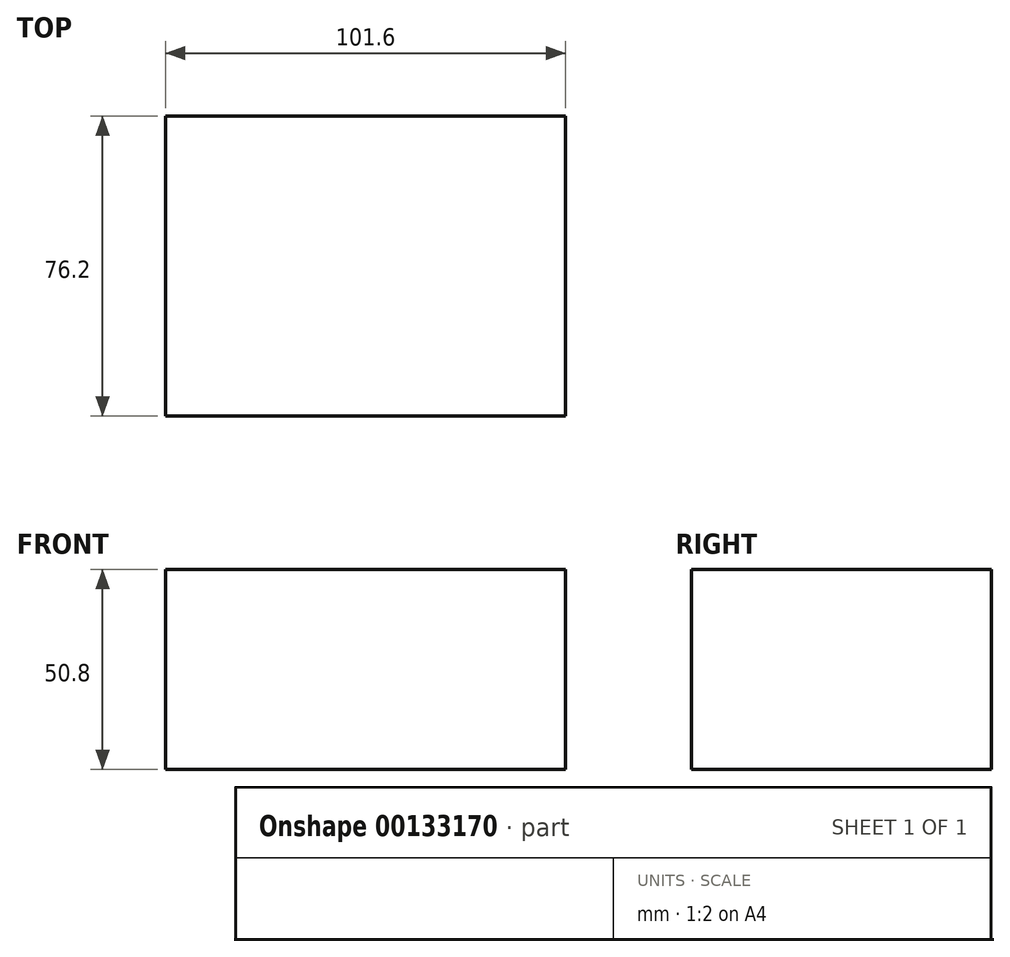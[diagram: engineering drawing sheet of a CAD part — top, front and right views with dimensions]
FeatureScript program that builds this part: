
annotation { "Feature Type Name" : "Feature", "Feature Type Description" : "" }
export const myFeature = defineFeature(function(context is Context, id is Id, definition is map)
    precondition{}
    {
        {
            var Q0;
            Q0=qCreatedBy(makeId("Front.planeOp"),FACE);
            var sketch = newSketch(context, id + "F0", { "sketchPlane" : qUnion([Q0])});
            skLineSegment(sketch, "E0.bottom", {"start": v(-50.8, -25.4) * mm, "end": v(50.8, -25.4) * mm});
            skLineSegment(sketch, "E0.top", {"start": v(-50.8, 25.4) * mm, "end": v(50.8, 25.4) * mm});
            skLineSegment(sketch, "E0.left", {"start": v(-50.8, -25.4) * mm, "end": v(-50.8, 25.4) * mm});
            skLineSegment(sketch, "E0.right", {"start": v(50.8, -25.4) * mm, "end": v(50.8, 25.4) * mm});
            skPoint(sketch, "E0.middle", {"position": v(0, 0) * mm});
            skSolve(sketch);
        }
        {
            var Q0;
            Q0=makeQuery(id+"F0.imprint","IMPRINT",FACE,{"disambiguationData":[TD([[makeQuery(id+"F0.imprint","IMPRINT",EDGE,{"derivedFrom":sQuery(id+"F0.wireOp",EDGE,"E0.bottom")}),1.0]])]});
            extrude(context, id + "F1", {"entities" : qUnion([Q0]), "endBound" : BoundingType.SYMMETRIC, "depth" : 76.2 * mm});
        }
    });
